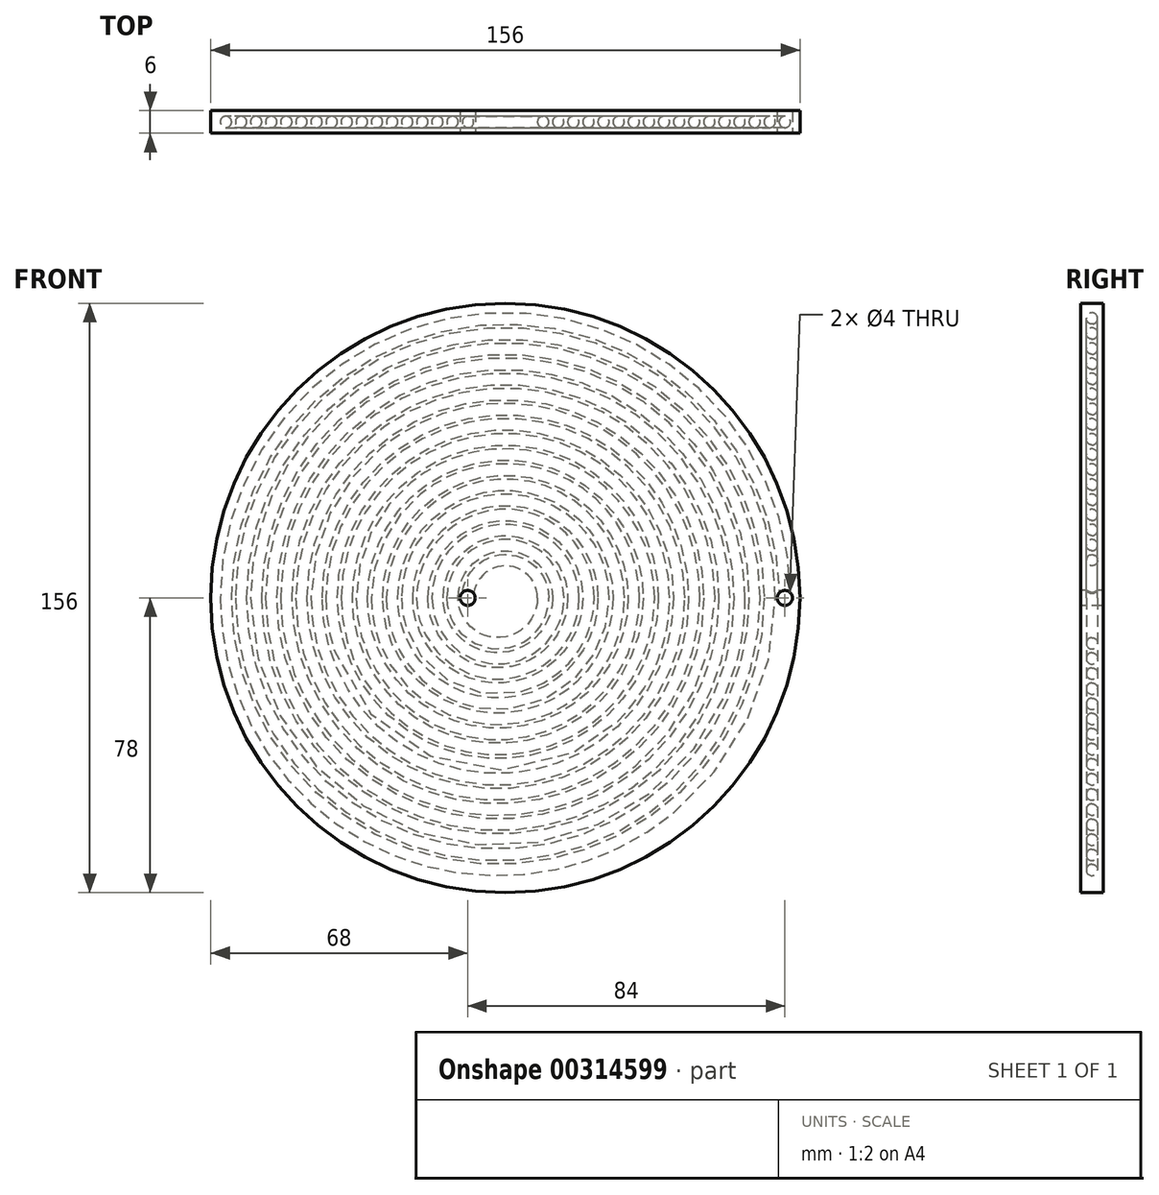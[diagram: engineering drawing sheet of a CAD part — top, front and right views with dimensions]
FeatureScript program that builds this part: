
annotation { "Feature Type Name" : "Feature", "Feature Type Description" : "" }
export const myFeature = defineFeature(function(context is Context, id is Id, definition is map)
    precondition{}
    {
        {
            var Q0;
            Q0=qCreatedBy(makeId("Top.planeOp"),FACE);
            var sketch = newSketch(context, id + "F0", { "sketchPlane" : qUnion([Q0])});
            skCircle(sketch, "E0", {"center": v(0, 0) * mm, "radius": 1.5 * mm});
            skSolve(sketch);
        }
        {
            var Q0;
            Q0=qCreatedBy(makeId("Front.planeOp"),FACE);
            var sketch = newSketch(context, id + "F1", { "sketchPlane" : qUnion([Q0])});
            skLineSegment(sketch, "E1", {"start": v(0, 0) * mm, "end": v(10, 0) * mm, "construction": true});
            skArc(sketch, "E2", {"start": v(20, 0) * mm, "mid": v(10, 10) * mm, "end": v(0, 0) * mm});
            skLineSegment(sketch, "E3", {"start": v(10, 0) * mm, "end": v(20, 0) * mm, "construction": true});
            skArc(sketch, "E4", {"start": v(-4, 0) * mm, "mid": v(10, 14) * mm, "end": v(24, 0) * mm});
            skArc(sketch, "E5", {"start": v(20, 0) * mm, "mid": v(8, -12) * mm, "end": v(-4, 0) * mm});
            skArc(sketch, "E6", {"start": v(24, 0) * mm, "mid": v(8, -16) * mm, "end": v(-8, 0) * mm});
            skArc(sketch, "E7", {"start": v(-8, 0) * mm, "mid": v(10, 18) * mm, "end": v(28, 0) * mm});
            skArc(sketch, "E8", {"start": v(28, 0) * mm, "mid": v(8, -20) * mm, "end": v(-12, 0) * mm});
            skArc(sketch, "E9", {"start": v(-12, 0) * mm, "mid": v(10, 22) * mm, "end": v(32, 0) * mm});
            skArc(sketch, "E10", {"start": v(32, 0) * mm, "mid": v(8, -24) * mm, "end": v(-16, 0) * mm});
            skArc(sketch, "E11", {"start": v(-16, 0) * mm, "mid": v(10, 26) * mm, "end": v(36, 0) * mm});
            skArc(sketch, "E12", {"start": v(36, 0) * mm, "mid": v(8, -28) * mm, "end": v(-20, 0) * mm});
            skArc(sketch, "E13", {"start": v(-20, 0) * mm, "mid": v(10, 30) * mm, "end": v(40, 0) * mm});
            skArc(sketch, "E14", {"start": v(40, 0) * mm, "mid": v(8, -32) * mm, "end": v(-24, 0) * mm});
            skArc(sketch, "E15", {"start": v(-24, 0) * mm, "mid": v(10, 34) * mm, "end": v(44, 0) * mm});
            skLineSegment(sketch, "E16", {"start": v(-24, 0) * mm, "end": v(-28, 0) * mm, "construction": true});
            skLineSegment(sketch, "E17", {"start": v(-28, 0) * mm, "end": v(-32, 0) * mm, "construction": true});
            skLineSegment(sketch, "E18", {"start": v(-40, 0) * mm, "end": v(-36, 0) * mm, "construction": true});
            skLineSegment(sketch, "E19", {"start": v(-32, 0) * mm, "end": v(-36, 0) * mm, "construction": true});
            skLineSegment(sketch, "E20", {"start": v(-40, 0) * mm, "end": v(-44, 0) * mm, "construction": true});
            skLineSegment(sketch, "E21", {"start": v(-44, 0) * mm, "end": v(-48, 0) * mm, "construction": true});
            skLineSegment(sketch, "E22", {"start": v(-48, 0) * mm, "end": v(-52, 0) * mm, "construction": true});
            skArc(sketch, "E23", {"start": v(-28, 0) * mm, "mid": v(10, 38) * mm, "end": v(48, 0) * mm});
            skArc(sketch, "E24", {"start": v(-32, 0) * mm, "mid": v(10, 42) * mm, "end": v(52, 0) * mm});
            skArc(sketch, "E25", {"start": v(-36, 0) * mm, "mid": v(10, 46) * mm, "end": v(56, 0) * mm});
            skArc(sketch, "E26", {"start": v(-40, 0) * mm, "mid": v(10, 50) * mm, "end": v(60, 0) * mm});
            skArc(sketch, "E27", {"start": v(-44, 0) * mm, "mid": v(10, 54) * mm, "end": v(64, 0) * mm});
            skArc(sketch, "E28", {"start": v(-48, 0) * mm, "mid": v(10, 58) * mm, "end": v(68, 0) * mm});
            skArc(sketch, "E29", {"start": v(-52, 0) * mm, "mid": v(10, 62) * mm, "end": v(72, 0) * mm});
            skArc(sketch, "E30", {"start": v(44, 0) * mm, "mid": v(8, -36) * mm, "end": v(-28, 0) * mm});
            skArc(sketch, "E31", {"start": v(48, 0) * mm, "mid": v(8, -40) * mm, "end": v(-32, 0) * mm});
            skArc(sketch, "E32", {"start": v(52, 0) * mm, "mid": v(8, -44) * mm, "end": v(-36, 0) * mm});
            skArc(sketch, "E33", {"start": v(56, 0) * mm, "mid": v(8, -48) * mm, "end": v(-40, 0) * mm});
            skArc(sketch, "E34", {"start": v(60, 0) * mm, "mid": v(8, -52) * mm, "end": v(-44, 0) * mm});
            skArc(sketch, "E35", {"start": v(64, 0) * mm, "mid": v(8, -56) * mm, "end": v(-48, 0) * mm});
            skArc(sketch, "E36", {"start": v(68, 0) * mm, "mid": v(8, -60) * mm, "end": v(-52, 0) * mm});
            skLineSegment(sketch, "E37", {"start": v(-52, 0) * mm, "end": v(-56, 0) * mm, "construction": true});
            skLineSegment(sketch, "E38", {"start": v(-56, 0) * mm, "end": v(-60, 0) * mm, "construction": true});
            skLineSegment(sketch, "E39", {"start": v(-60, 0) * mm, "end": v(-64, 0) * mm, "construction": true});
            skLineSegment(sketch, "E40", {"start": v(-64, 0) * mm, "end": v(-68, 0) * mm, "construction": true});
            skLineSegment(sketch, "E41", {"start": v(-68, 0) * mm, "end": v(-72, 0) * mm, "construction": true});
            skLineSegment(sketch, "E42", {"start": v(-72, 0) * mm, "end": v(-76, 0) * mm, "construction": true});
            skLineSegment(sketch, "E43", {"start": v(-76, 0) * mm, "end": v(-80, 0) * mm, "construction": true});
            skLineSegment(sketch, "E44", {"start": v(-80, 0) * mm, "end": v(-84, 0) * mm, "construction": true});
            skArc(sketch, "E45", {"start": v(-56, 0) * mm, "mid": v(10, 66) * mm, "end": v(76, 0) * mm});
            skArc(sketch, "E46", {"start": v(-60, 0) * mm, "mid": v(10, 70) * mm, "end": v(80, 0) * mm});
            skArc(sketch, "E47", {"start": v(-64, 0) * mm, "mid": v(10, 74) * mm, "end": v(84, 0) * mm});
            skArc(sketch, "E48", {"start": v(72, 0) * mm, "mid": v(8, -64) * mm, "end": v(-56, 0) * mm});
            skArc(sketch, "E49", {"start": v(76, 0) * mm, "mid": v(8, -68) * mm, "end": v(-60, 0) * mm});
            skArc(sketch, "E50", {"start": v(80, 0) * mm, "mid": v(8, -72) * mm, "end": v(-64, 0) * mm});
            skSolve(sketch);
        }
        {
            var Q0;
            Q0=qCreatedBy(makeId("Front.planeOp"),FACE);
            cPlane(context, id + "F2", {"entities" : qUnion([Q0]), "cplaneType" : CPlaneType.OFFSET, "offset" : 3 * mm, "width" : 152.4 * mm, "height" : 152.4 * mm});
        }
        {
            var Q0;
            Q0=qCreatedBy(id+"F2.planeOp",FACE);
            var sketch = newSketch(context, id + "F3", { "sketchPlane" : qUnion([Q0])});
            skCircle(sketch, "E51", {"center": v(10, 0) * mm, "radius": 78 * mm});
            skCircle(sketch, "E52", {"center": v(0, 0) * mm, "radius": 2 * mm});
            skCircle(sketch, "E53", {"center": v(84, 0) * mm, "radius": 2 * mm});
            skLineSegment(sketch, "E54", {"start": v(0, 0) * mm, "end": v(10, 0) * mm, "construction": true});
            skSolve(sketch);
        }
        {
            var Q0;
            Q0=makeQuery(id+"F3.imprint","IMPRINT",FACE,{"disambiguationData":[TD([[makeQuery(id+"F3.imprint","IMPRINT",EDGE,{"derivedFrom":sQuery(id+"F3.wireOp",EDGE,"E51")}),1.0]])]});
            extrude(context, id + "F4", {"entities" : qUnion([Q0]), "oppositeDirection" : true, "depth" : 6 * mm});
        }
        {
            var Q0;
            Q0 = qSketchRegion(id + "F0", true);
            var Q1;
            Q1 = qConstructionFilter(qBodyType(qCreatedBy(id + "F1" ,EDGE), BodyType.WIRE), ConstructionObject.NO);
            sweep(context, id + "F5", {"operationType" : NewBodyOperationType.REMOVE, "profiles" : qUnion([Q0]), "path" : qUnion([Q1])});
        }
    });
